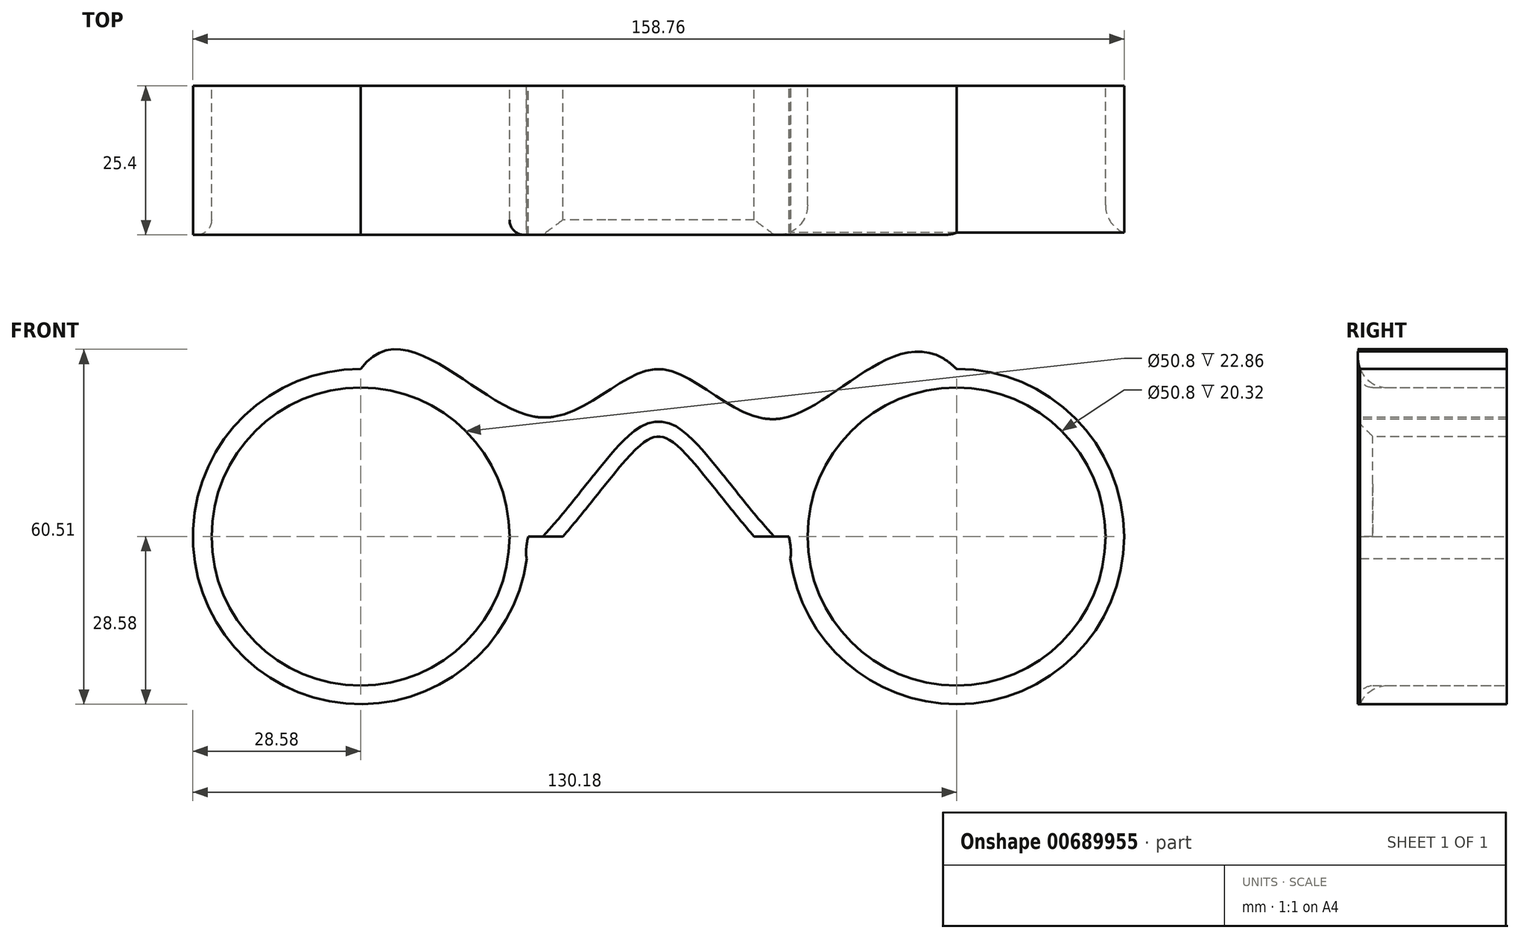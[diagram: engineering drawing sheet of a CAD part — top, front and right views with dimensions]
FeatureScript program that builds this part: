
annotation { "Feature Type Name" : "Feature", "Feature Type Description" : "" }
export const myFeature = defineFeature(function(context is Context, id is Id, definition is map)
    precondition{}
    {
        {
            var Q0;
            Q0=qCreatedBy(makeId("Front.planeOp"),FACE);
            var sketch = newSketch(context, id + "F0", { "sketchPlane" : qUnion([Q0])});
            skCircle(sketch, "E0", {"center": v(-50.8, 0) * mm, "radius": 28.58 * mm});
            skCircle(sketch, "E1", {"center": v(-50.8, 0) * mm, "radius": 25.4 * mm});
            skCircle(sketch, "E2", {"center": v(50.8, 0) * mm, "radius": 28.58 * mm});
            skCircle(sketch, "E3", {"center": v(50.8, 0) * mm, "radius": 25.4 * mm});
            skLineSegment(sketch, "E4", {"start": v(0, 0) * mm, "end": v(-50.8, 0) * mm});
            skLineSegment(sketch, "E5", {"start": v(0, 0) * mm, "end": v(50.8, 0) * mm});
            skLineSegment(sketch, "E6", {"start": v(-50.8, 0) * mm, "end": v(-50.8, 28.57) * mm});
            skLineSegment(sketch, "E7", {"start": v(50.8, 0) * mm, "end": v(50.8, 28.58) * mm});
            skFitSpline(sketch, "E8", {"points": [v(-50.8, 28.57) * mm, v(-21.24, 20.45) * mm, v(0, 28.58) * mm, v(20.92, 20.14) * mm, v(50.8, 28.58) * mm], "startDerivative": vector(85.57, 115.77) * mm, "endDerivative": vector(105.25, -106.2) * mm});
            skFitSpline(sketch, "E9", {"points": [v(-22.23, 0) * mm, v(-8.98, 8.98) * mm, v(0, 17.05) * mm, v(8.98, 8.98) * mm, v(22.23, 0) * mm], "startDerivative": vector(-26.25, -127) * mm, "endDerivative": vector(-26.25, 127) * mm});
            skLineSegment(sketch, "E10", {"start": v(-8.98, 8.98) * mm, "end": v(8.98, 8.98) * mm});
            skLineSegment(sketch, "E11", {"start": v(-24.57, -11.33) * mm, "end": v(24.57, -11.33) * mm});
            skLineSegment(sketch, "E12", {"start": v(-8.98, 8.98) * mm, "end": v(0, 0) * mm});
            skLineSegment(sketch, "E13", {"start": v(8.98, 8.98) * mm, "end": v(0, 0) * mm});
            skLineSegment(sketch, "E14", {"start": v(50.8, 0) * mm, "end": v(79.38, 0) * mm});
            skLineSegment(sketch, "E15", {"start": v(-50.8, 0) * mm, "end": v(-79.38, 0) * mm});
            skLineSegment(sketch, "E16", {"start": v(-21.24, 20.45) * mm, "end": v(20.92, 20.14) * mm});
            skSolve(sketch);
        }
        {
            var Q0;
            {var subQ0=sQuery(id+"F0.wireOp",EDGE,"E6");var subQ5=sQuery(id+"F0.wireOp",EDGE,"E1");var subQ6=makeQuery(id+"F0.imprint","INTERSECT",VERTEX,{"derivedFrom":[subQ5,subQ0]});Q0=makeQuery(id+"F0.imprint","IMPRINT",FACE,{"disambiguationData":[TD([[makeQuery(id+"F0.imprint","IMPRINT",EDGE,{"disambiguationData":[TD([[subQ6,1.0]])],"derivedFrom":subQ5}),-1.0]])]});}
            var Q1;
            {var subQ2=sQuery(id+"F0.wireOp",EDGE,"E0");var subQ8=makeQuery(id+"F0.imprint","INTERSECT",VERTEX,{"derivedFrom":[subQ2,sQuery(id+"F0.wireOp",EDGE,"E11")]});Q1=makeQuery(id+"F0.imprint","IMPRINT",FACE,{"disambiguationData":[TD([[makeQuery(id+"F0.imprint","IMPRINT",EDGE,{"disambiguationData":[TD([[subQ8,1.0]])],"derivedFrom":subQ2}),1.0]])]});}
            var Q2;
            {var subQ0=sQuery(id+"F0.wireOp",EDGE,"E6");var subQ5=sQuery(id+"F0.wireOp",EDGE,"E1");var subQ6=makeQuery(id+"F0.imprint","INTERSECT",VERTEX,{"derivedFrom":[subQ5,subQ0]});Q2=makeQuery(id+"F0.imprint","IMPRINT",FACE,{"disambiguationData":[TD([[makeQuery(id+"F0.imprint","IMPRINT",EDGE,{"disambiguationData":[TD([[subQ6,-1.0]])],"derivedFrom":subQ5}),-1.0]])]});}
            var Q3;
            {var subQ6=sQuery(id+"F0.wireOp",EDGE,"E16");var subQ7=sQuery(id+"F0.wireOp",EDGE,"E8");var subQ8=makeQuery(id+"F0.imprint","INTERSECT",VERTEX,{"disambiguationData":[OD(0.0)],"derivedFrom":[subQ7,subQ6]});Q3=makeQuery(id+"F0.imprint","IMPRINT",FACE,{"disambiguationData":[TD([[makeQuery(id+"F0.imprint","IMPRINT",EDGE,{"disambiguationData":[TD([[subQ8,-1.0]])],"derivedFrom":subQ7}),-1.0]])]});}
            var Q4;
            {var subQ0=sQuery(id+"F0.wireOp",EDGE,"E16");var subQ1=sQuery(id+"F0.wireOp",EDGE,"E8");var subQ2=makeQuery(id+"F0.imprint","INTERSECT",VERTEX,{"disambiguationData":[OD(2.0)],"derivedFrom":[subQ1,subQ0]});Q4=makeQuery(id+"F0.imprint","IMPRINT",FACE,{"disambiguationData":[TD([[makeQuery(id+"F0.imprint","IMPRINT",EDGE,{"disambiguationData":[TD([[subQ2,-1.0]])],"derivedFrom":subQ1}),-1.0]])]});}
            var Q5;
            {var subQ0=sQuery(id+"F0.wireOp",EDGE,"E7");var subQ5=sQuery(id+"F0.wireOp",EDGE,"E3");var subQ6=makeQuery(id+"F0.imprint","INTERSECT",VERTEX,{"derivedFrom":[subQ5,subQ0]});Q5=makeQuery(id+"F0.imprint","IMPRINT",FACE,{"disambiguationData":[TD([[makeQuery(id+"F0.imprint","IMPRINT",EDGE,{"disambiguationData":[TD([[subQ6,-1.0]])],"derivedFrom":subQ5}),-1.0]])]});}
            var Q6;
            {var subQ0=sQuery(id+"F0.wireOp",EDGE,"E7");var subQ5=sQuery(id+"F0.wireOp",EDGE,"E3");var subQ6=makeQuery(id+"F0.imprint","INTERSECT",VERTEX,{"derivedFrom":[subQ5,subQ0]});Q6=makeQuery(id+"F0.imprint","IMPRINT",FACE,{"disambiguationData":[TD([[makeQuery(id+"F0.imprint","IMPRINT",EDGE,{"disambiguationData":[TD([[subQ6,1.0]])],"derivedFrom":subQ5}),-1.0]])]});}
            var Q7;
            {var subQ6=sQuery(id+"F0.wireOp",EDGE,"E2");var subQ8=makeQuery(id+"F0.imprint","INTERSECT",VERTEX,{"derivedFrom":[subQ6,sQuery(id+"F0.wireOp",EDGE,"E11")]});Q7=makeQuery(id+"F0.imprint","IMPRINT",FACE,{"disambiguationData":[TD([[makeQuery(id+"F0.imprint","IMPRINT",EDGE,{"disambiguationData":[TD([[subQ8,1.0]])],"derivedFrom":subQ6}),1.0]])]});}
            extrude(context, id + "F1", {"entities" : qUnion([Q0, Q1, Q2, Q3, Q4, Q5, Q6, Q7]), "depth" : 25.4 * mm, "offsetDistance" : 25.4 * mm});
        }
        {
            var Q0;
            Q0=makeQuery(id+"F1.opExtrude","CAP_EDGE",EDGE,{"disambiguationData":[OSD([sQuery(id+"F0.wireOp",EDGE,"E1")])],"isStart":false});
            fillet(context, id + "F2", {"entities" : qUnion([Q0]), "radius" : 2.54 * mm, "tangentPropagation" : true, "allowEdgeOverflow" : false});
        }
        {
            var Q0;
            Q0=makeQuery(id+"F1.opExtrude","CAP_EDGE",EDGE,{"disambiguationData":[OSD([sQuery(id+"F0.wireOp",EDGE,"E3")])],"isStart":false});
            fillet(context, id + "F3", {"entities" : qUnion([Q0]), "radius" : 5.08 * mm, "tangentPropagation" : true, "allowEdgeOverflow" : false});
        }
        {
            var Q0;
            {var subQ0=sQuery(id+"F0.wireOp",EDGE,"E10");var subQ1=sQuery(id+"F0.wireOp",EDGE,"E9");var subQ3=makeQuery(id+"F0.imprint","INTERSECT",VERTEX,{"derivedFrom":[subQ1,subQ0,sQuery(id+"F0.wireOp",EDGE,"E12")]});Q0=makeQuery(id+"F1.opExtrude","CAP_EDGE",EDGE,{"disambiguationData":[OSD([subQ1]),TDD([makeQuery(id+"F0.imprint","IMPRINT",EDGE,{"disambiguationData":[TD([[makeQuery(id+"F0.imprint","INTERSECT",VERTEX,{"derivedFrom":[sQuery(id+"F0.wireOp",EDGE,"E4"),subQ1]}),-1.0]])],"derivedFrom":subQ1}),makeQuery(id+"F0.imprint","IMPRINT",EDGE,{"disambiguationData":[TD([[subQ3,-1.0]])],"derivedFrom":subQ1}),makeQuery(id+"F0.imprint","IMPRINT",EDGE,{"disambiguationData":[TD([[makeQuery(id+"F0.imprint","INTERSECT",VERTEX,{"derivedFrom":[sQuery(id+"F0.wireOp",EDGE,"E5"),subQ1]}),1.0]])],"derivedFrom":subQ1})])],"isStart":false});}
            chamfer(context, id + "F4", {"entities" : qUnion([Q0]), "width" : 2.54 * mm, "tangentPropagation" : true});
        }
    });
